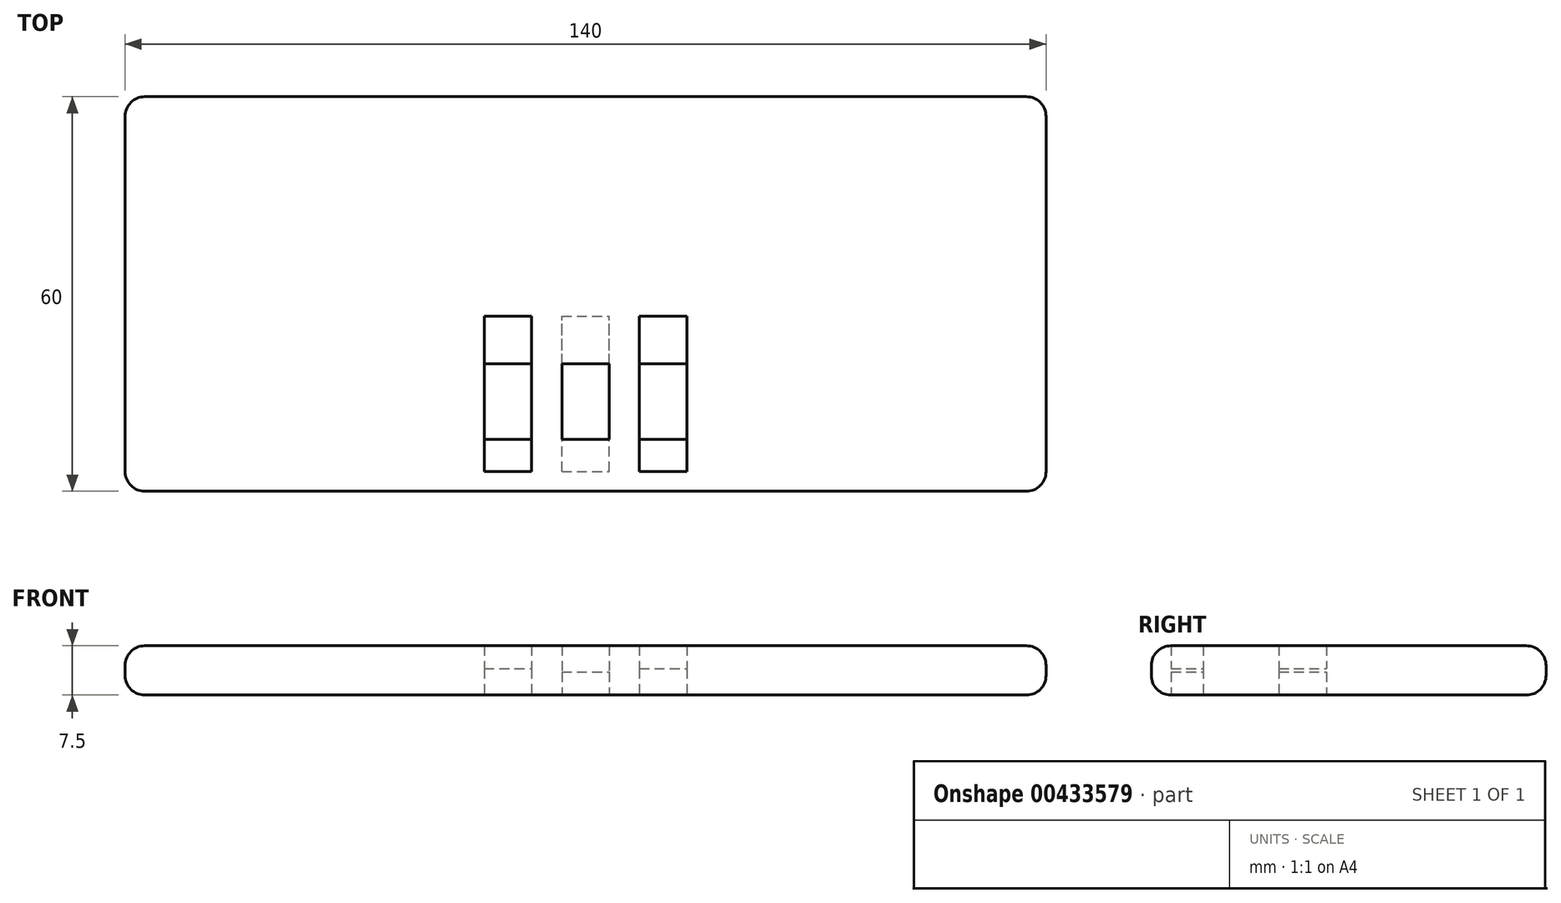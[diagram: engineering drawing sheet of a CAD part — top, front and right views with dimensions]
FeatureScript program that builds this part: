
annotation { "Feature Type Name" : "Feature", "Feature Type Description" : "" }
export const myFeature = defineFeature(function(context is Context, id is Id, definition is map)
    precondition{}
    {
        {
            var Q0;
            Q0=qCreatedBy(makeId("Top.planeOp"),FACE);
            var sketch = newSketch(context, id + "F0", { "sketchPlane" : qUnion([Q0])});
            skLineSegment(sketch, "E0.bottom", {"start": v(70, 30) * mm, "end": v(-70, 30) * mm});
            skLineSegment(sketch, "E0.top", {"start": v(70, -30) * mm, "end": v(-70, -30) * mm});
            skLineSegment(sketch, "E0.left", {"start": v(70, 30) * mm, "end": v(70, -30) * mm});
            skLineSegment(sketch, "E0.right", {"start": v(-70, 30) * mm, "end": v(-70, -30) * mm});
            skPoint(sketch, "E0.middle", {"position": v(0, 0) * mm});
            skSolve(sketch);
        }
        {
            var Q0;
            Q0 = qSketchRegion(id + "F0", true);
            extrude(context, id + "F1", {"entities" : qUnion([Q0]), "depth" : 7.5 * mm});
        }
        {
            var Q0;
            Q0=makeQuery(id+"F1.opExtrude","CAP_EDGE",EDGE,{"disambiguationData":[OSD([sQuery(id+"F0.wireOp",EDGE,"E0.top")])],"isStart":false});
            var Q1;
            Q1=makeQuery(id+"F1.opExtrude","CAP_EDGE",EDGE,{"disambiguationData":[OSD([sQuery(id+"F0.wireOp",EDGE,"E0.left")])],"isStart":false});
            var Q2;
            Q2=makeQuery(id+"F1.opExtrude","CAP_EDGE",EDGE,{"disambiguationData":[OSD([sQuery(id+"F0.wireOp",EDGE,"E0.bottom")])],"isStart":false});
            var Q3;
            Q3=makeQuery(id+"F1.opExtrude","CAP_EDGE",EDGE,{"disambiguationData":[OSD([sQuery(id+"F0.wireOp",EDGE,"E0.right")])],"isStart":false});
            var Q4;
            Q4=makeQuery(id+"F1.opExtrude","CAP_EDGE",EDGE,{"disambiguationData":[OSD([sQuery(id+"F0.wireOp",EDGE,"E0.bottom")])],"isStart":true});
            var Q5;
            Q5=makeQuery(id+"F1.opExtrude","SWEPT_EDGE",EDGE,{"disambiguationData":[OSD([sQuery(id+"F0.wireOp",EDGE,"E0.bottom"),sQuery(id+"F0.wireOp",EDGE,"E0.left")])]});
            var Q6;
            Q6=makeQuery(id+"F1.opExtrude","CAP_EDGE",EDGE,{"disambiguationData":[OSD([sQuery(id+"F0.wireOp",EDGE,"E0.left")])],"isStart":true});
            var Q7;
            Q7=makeQuery(id+"F1.opExtrude","SWEPT_EDGE",EDGE,{"disambiguationData":[OSD([sQuery(id+"F0.wireOp",EDGE,"E0.top"),sQuery(id+"F0.wireOp",EDGE,"E0.left")])]});
            var Q8;
            Q8=makeQuery(id+"F1.opExtrude","SWEPT_EDGE",EDGE,{"disambiguationData":[OSD([sQuery(id+"F0.wireOp",EDGE,"E0.bottom"),sQuery(id+"F0.wireOp",EDGE,"E0.right")])]});
            var Q9;
            Q9=makeQuery(id+"F1.opExtrude","CAP_EDGE",EDGE,{"disambiguationData":[OSD([sQuery(id+"F0.wireOp",EDGE,"E0.right")])],"isStart":true});
            var Q10;
            Q10=makeQuery(id+"F1.opExtrude","CAP_EDGE",EDGE,{"disambiguationData":[OSD([sQuery(id+"F0.wireOp",EDGE,"E0.top")])],"isStart":true});
            var Q11;
            Q11=makeQuery(id+"F1.opExtrude","SWEPT_FACE",FACE,{"disambiguationData":[OSD([sQuery(id+"F0.wireOp",EDGE,"E0.top")])]});
            var Q12;
            Q12=makeQuery(id+"F1.opExtrude","SWEPT_EDGE",EDGE,{"disambiguationData":[OSD([sQuery(id+"F0.wireOp",EDGE,"E0.top"),sQuery(id+"F0.wireOp",EDGE,"E0.right")])]});
            fillet(context, id + "F2", {"entities" : qUnion([Q0, Q1, Q2, Q3, Q4, Q5, Q6, Q7, Q8, Q9, Q10, Q11, Q12]), "radius" : 3 * mm, "tangentPropagation" : true, "allowEdgeOverflow" : false});
        }
        {
            var Q0;
            Q0=qCreatedBy(makeId("Top.planeOp"),FACE);
            var sketch = newSketch(context, id + "F3", { "sketchPlane" : qUnion([Q0])});
            skLineSegment(sketch, "E1.bottom", {"start": v(-3.6, -27) * mm, "end": v(3.6, -27) * mm});
            skLineSegment(sketch, "E1.top", {"start": v(-3.6, -3.4) * mm, "end": v(3.6, -3.4) * mm});
            skLineSegment(sketch, "E1.left", {"start": v(-3.6, -27) * mm, "end": v(-3.6, -3.4) * mm});
            skLineSegment(sketch, "E1.right", {"start": v(3.6, -27) * mm, "end": v(3.6, -3.4) * mm});
            skLineSegment(sketch, "E2.bottom", {"start": v(-3.6, -22.1) * mm, "end": v(3.6, -22.1) * mm});
            skLineSegment(sketch, "E2.top", {"start": v(-3.6, -10.6) * mm, "end": v(3.6, -10.6) * mm});
            skLineSegment(sketch, "E2.left", {"start": v(-3.6, -22.1) * mm, "end": v(-3.6, -10.6) * mm});
            skLineSegment(sketch, "E2.right", {"start": v(3.6, -22.1) * mm, "end": v(3.6, -10.6) * mm});
            skLineSegment(sketch, "E3.bottom", {"start": v(-15.4, -27) * mm, "end": v(-8.2, -27) * mm});
            skLineSegment(sketch, "E3.top", {"start": v(-15.4, -3.4) * mm, "end": v(-8.2, -3.4) * mm});
            skLineSegment(sketch, "E3.left", {"start": v(-15.4, -27) * mm, "end": v(-15.4, -3.4) * mm});
            skLineSegment(sketch, "E3.right", {"start": v(-8.2, -27) * mm, "end": v(-8.2, -3.4) * mm});
            skLineSegment(sketch, "E4.bottom", {"start": v(-15.4, -22.1) * mm, "end": v(-8.2, -22.1) * mm});
            skLineSegment(sketch, "E4.top", {"start": v(-15.4, -10.6) * mm, "end": v(-8.2, -10.6) * mm});
            skLineSegment(sketch, "E4.left", {"start": v(-15.4, -22.1) * mm, "end": v(-15.4, -10.6) * mm});
            skLineSegment(sketch, "E4.right", {"start": v(-8.2, -22.1) * mm, "end": v(-8.2, -10.6) * mm});
            skLineSegment(sketch, "E5.bottom", {"start": v(8.2, -27) * mm, "end": v(15.4, -27) * mm});
            skLineSegment(sketch, "E5.top", {"start": v(8.2, -3.4) * mm, "end": v(15.4, -3.4) * mm});
            skLineSegment(sketch, "E5.left", {"start": v(8.2, -27) * mm, "end": v(8.2, -3.4) * mm});
            skLineSegment(sketch, "E5.right", {"start": v(15.4, -27) * mm, "end": v(15.4, -3.4) * mm});
            skLineSegment(sketch, "E6.bottom", {"start": v(8.2, -22.1) * mm, "end": v(15.4, -22.1) * mm});
            skLineSegment(sketch, "E6.top", {"start": v(8.2, -10.6) * mm, "end": v(15.4, -10.6) * mm});
            skLineSegment(sketch, "E6.left", {"start": v(8.2, -22.1) * mm, "end": v(8.2, -10.6) * mm});
            skLineSegment(sketch, "E6.right", {"start": v(15.4, -22.1) * mm, "end": v(15.4, -10.6) * mm});
            skSolve(sketch);
        }
        {
            var Q0;
            {var subQ0=sQuery(id+"F3.wireOp",EDGE,"E1.top");Q0=makeQuery(id+"F3.imprint","IMPRINT",FACE,{"disambiguationData":[TD([[makeQuery(id+"F3.imprint","IMPRINT",EDGE,{"derivedFrom":subQ0}),-1.0]])]});}
            var Q1;
            {var subQ0=sQuery(id+"F3.wireOp",EDGE,"E1.bottom");Q1=makeQuery(id+"F3.imprint","IMPRINT",FACE,{"disambiguationData":[TD([[makeQuery(id+"F3.imprint","IMPRINT",EDGE,{"derivedFrom":subQ0}),1.0]])]});}
            extrude(context, id + "F4", {"entities" : qUnion([Q0, Q1]), "operationType" : NewBodyOperationType.REMOVE, "depth" : 3.5 * mm});
        }
        {
            var Q0;
            Q0=makeQuery(id+"F3.imprint","IMPRINT",FACE,{"disambiguationData":[TD([[makeQuery(id+"F3.imprint","IMPRINT",EDGE,{"derivedFrom":sQuery(id+"F3.wireOp",EDGE,"E2.bottom")}),1.0]])]});
            extrude(context, id + "F5", {"entities" : qUnion([Q0]), "operationType" : NewBodyOperationType.REMOVE, "oppositeDirection" : true, "depth" : -10 * mm});
        }
        {
            var Q0;
            Q0=makeQuery(id+"F3.imprint","IMPRINT",FACE,{"disambiguationData":[TD([[makeQuery(id+"F3.imprint","IMPRINT",EDGE,{"derivedFrom":sQuery(id+"F3.wireOp",EDGE,"E4.bottom")}),1.0]])]});
            var Q1;
            Q1=makeQuery(id+"F3.imprint","IMPRINT",FACE,{"disambiguationData":[TD([[makeQuery(id+"F3.imprint","IMPRINT",EDGE,{"derivedFrom":sQuery(id+"F3.wireOp",EDGE,"E6.bottom")}),1.0]])]});
            extrude(context, id + "F6", {"entities" : qUnion([Q0, Q1]), "operationType" : NewBodyOperationType.REMOVE, "depth" : 25 * mm});
        }
        {
            var Q0;
            {var subQ0=sQuery(id+"F3.wireOp",EDGE,"E3.bottom");Q0=makeQuery(id+"F3.imprint","IMPRINT",FACE,{"disambiguationData":[TD([[makeQuery(id+"F3.imprint","IMPRINT",EDGE,{"derivedFrom":subQ0}),1.0]])]});}
            var Q1;
            {var subQ0=sQuery(id+"F3.wireOp",EDGE,"E3.top");Q1=makeQuery(id+"F3.imprint","IMPRINT",FACE,{"disambiguationData":[TD([[makeQuery(id+"F3.imprint","IMPRINT",EDGE,{"derivedFrom":subQ0}),-1.0]])]});}
            var Q2;
            {var subQ0=sQuery(id+"F3.wireOp",EDGE,"E5.top");Q2=makeQuery(id+"F3.imprint","IMPRINT",FACE,{"disambiguationData":[TD([[makeQuery(id+"F3.imprint","IMPRINT",EDGE,{"derivedFrom":subQ0}),-1.0]])]});}
            var Q3;
            {var subQ0=sQuery(id+"F3.wireOp",EDGE,"E5.bottom");Q3=makeQuery(id+"F3.imprint","IMPRINT",FACE,{"disambiguationData":[TD([[makeQuery(id+"F3.imprint","IMPRINT",EDGE,{"derivedFrom":subQ0}),1.0]])]});}
            extrude(context, id + "F7", {"entities" : qUnion([Q0, Q1, Q2, Q3]), "operationType" : NewBodyOperationType.REMOVE, "depth" : 10 * mm, "hasSecondDirection" : true, "secondDirectionOppositeDirection" : false, "secondDirectionDepth" : 4 * mm});
        }
    });
